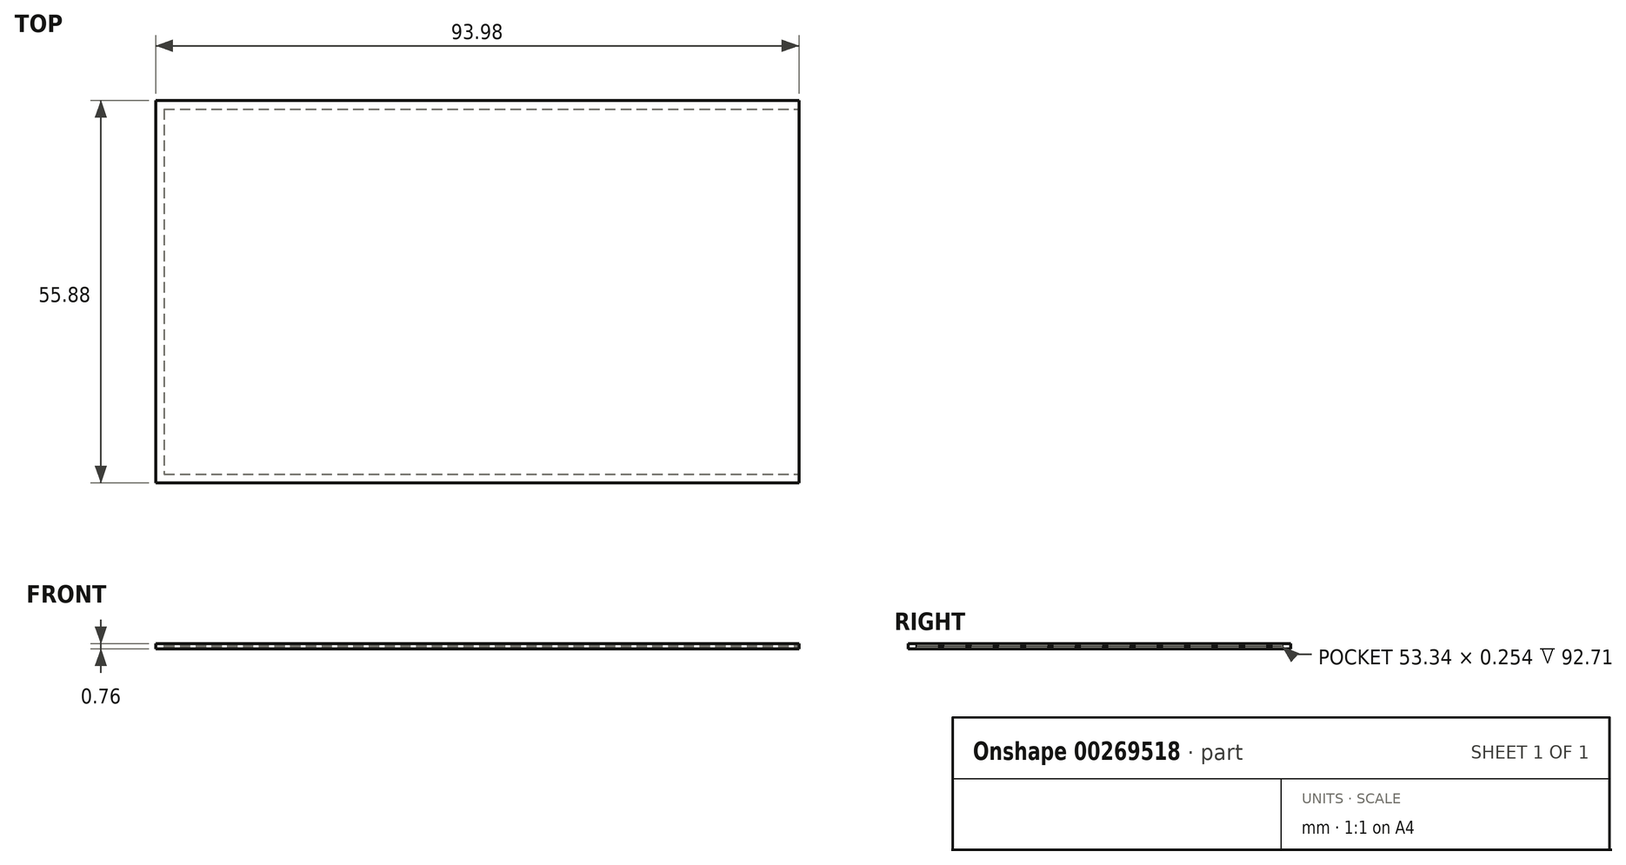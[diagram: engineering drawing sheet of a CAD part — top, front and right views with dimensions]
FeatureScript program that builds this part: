
annotation { "Feature Type Name" : "Feature", "Feature Type Description" : "" }
export const myFeature = defineFeature(function(context is Context, id is Id, definition is map)
    precondition{}
    {
        {
            var Q0;
            Q0=qCreatedBy(makeId("Top.planeOp"),FACE);
            var sketch = newSketch(context, id + "F0", { "sketchPlane" : qUnion([Q0])});
            skLineSegment(sketch, "E0.bottom", {"start": v(-50.27, 9.92) * mm, "end": v(43.7, 9.92) * mm});
            skLineSegment(sketch, "E0.top", {"start": v(-50.27, -45.96) * mm, "end": v(43.7, -45.96) * mm});
            skLineSegment(sketch, "E0.left", {"start": v(-50.27, 9.92) * mm, "end": v(-50.27, -45.96) * mm});
            skLineSegment(sketch, "E0.right", {"start": v(43.7, 9.92) * mm, "end": v(43.7, -45.96) * mm});
            skSolve(sketch);
        }
        {
            var Q0;
            Q0 = qSketchRegion(id + "F0", true);
            extrude(context, id + "F1", {"entities" : qUnion([Q0]), "depth" : 0.25 * mm});
        }
        {
            var Q0;
            Q0=makeQuery(id+"F1.opExtrude","CAP_FACE",FACE,{"disambiguationData":[OSD([sQuery(id+"F0.wireOp",EDGE,"E0.bottom"),sQuery(id+"F0.wireOp",EDGE,"E0.top"),sQuery(id+"F0.wireOp",EDGE,"E0.left"),sQuery(id+"F0.wireOp",EDGE,"E0.right")])],"isStart":false});
            var sketch = newSketch(context, id + "F2", { "sketchPlane" : qUnion([Q0])});
            skLineSegment(sketch, "E1.1", {"start": v(-50.27, 9.92) * mm, "end": v(-50.27, -45.96) * mm});
            skLineSegment(sketch, "E1.2", {"start": v(-50.27, -45.96) * mm, "end": v(43.7, -45.96) * mm});
            skLineSegment(sketch, "E2.0", {"start": v(-50.27, 9.92) * mm, "end": v(43.7, 9.92) * mm});
            skLineSegment(sketch, "E3.0", {"start": v(-49, -44.7) * mm, "end": v(43.7, -44.7) * mm});
            skLineSegment(sketch, "E3.1", {"start": v(-49, 8.65) * mm, "end": v(-49, -44.7) * mm});
            skLineSegment(sketch, "E3.2", {"start": v(-49, 8.65) * mm, "end": v(43.7, 8.65) * mm});
            skLineSegment(sketch, "E4", {"start": v(43.7, 8.65) * mm, "end": v(43.7, 9.92) * mm});
            skLineSegment(sketch, "E5", {"start": v(43.7, -44.7) * mm, "end": v(43.7, -45.96) * mm});
            skSolve(sketch);
        }
        {
            var Q0;
            Q0=makeQuery(id+"F2.imprint","IMPRINT",FACE,{"disambiguationData":[TD([[makeQuery(id+"F2.imprint","IMPRINT",EDGE,{"derivedFrom":sQuery(id+"F2.wireOp",EDGE,"E1.1")}),1.0]])]});
            extrude(context, id + "F3", {"entities" : qUnion([Q0]), "operationType" : NewBodyOperationType.ADD, "depth" : 0.25 * mm});
        }
        {
            var Q0;
            Q0=makeQuery(id+"F3.opExtrude","CAP_FACE",FACE,{"disambiguationData":[OSD([sQuery(id+"F2.wireOp",EDGE,"E1.1"),sQuery(id+"F2.wireOp",EDGE,"E1.2"),sQuery(id+"F2.wireOp",EDGE,"E2.0"),sQuery(id+"F2.wireOp",EDGE,"E3.0"),sQuery(id+"F2.wireOp",EDGE,"E3.1"),sQuery(id+"F2.wireOp",EDGE,"E3.2"),sQuery(id+"F2.wireOp",EDGE,"E4"),sQuery(id+"F2.wireOp",EDGE,"E5")])],"isStart":false});
            var sketch = newSketch(context, id + "F4", { "sketchPlane" : qUnion([Q0])});
            skLineSegment(sketch, "E6.0", {"start": v(-50.27, -45.96) * mm, "end": v(43.7, -45.96) * mm});
            skLineSegment(sketch, "E6.1", {"start": v(-50.27, 9.92) * mm, "end": v(43.7, 9.92) * mm});
            skLineSegment(sketch, "E6.2", {"start": v(-50.27, 9.92) * mm, "end": v(-50.27, -45.96) * mm});
            skLineSegment(sketch, "E6.3", {"start": v(43.7, 8.65) * mm, "end": v(43.7, -44.7) * mm});
            skLineSegment(sketch, "E6.4", {"start": v(43.7, -44.7) * mm, "end": v(43.7, -45.96) * mm});
            skLineSegment(sketch, "E6.5", {"start": v(43.7, 9.92) * mm, "end": v(43.7, 8.65) * mm});
            skSolve(sketch);
        }
        {
            var Q0;
            Q0 = qSketchRegion(id + "F4", true);
            extrude(context, id + "F5", {"entities" : qUnion([Q0]), "operationType" : NewBodyOperationType.ADD, "depth" : 0.25 * mm});
        }
    });
